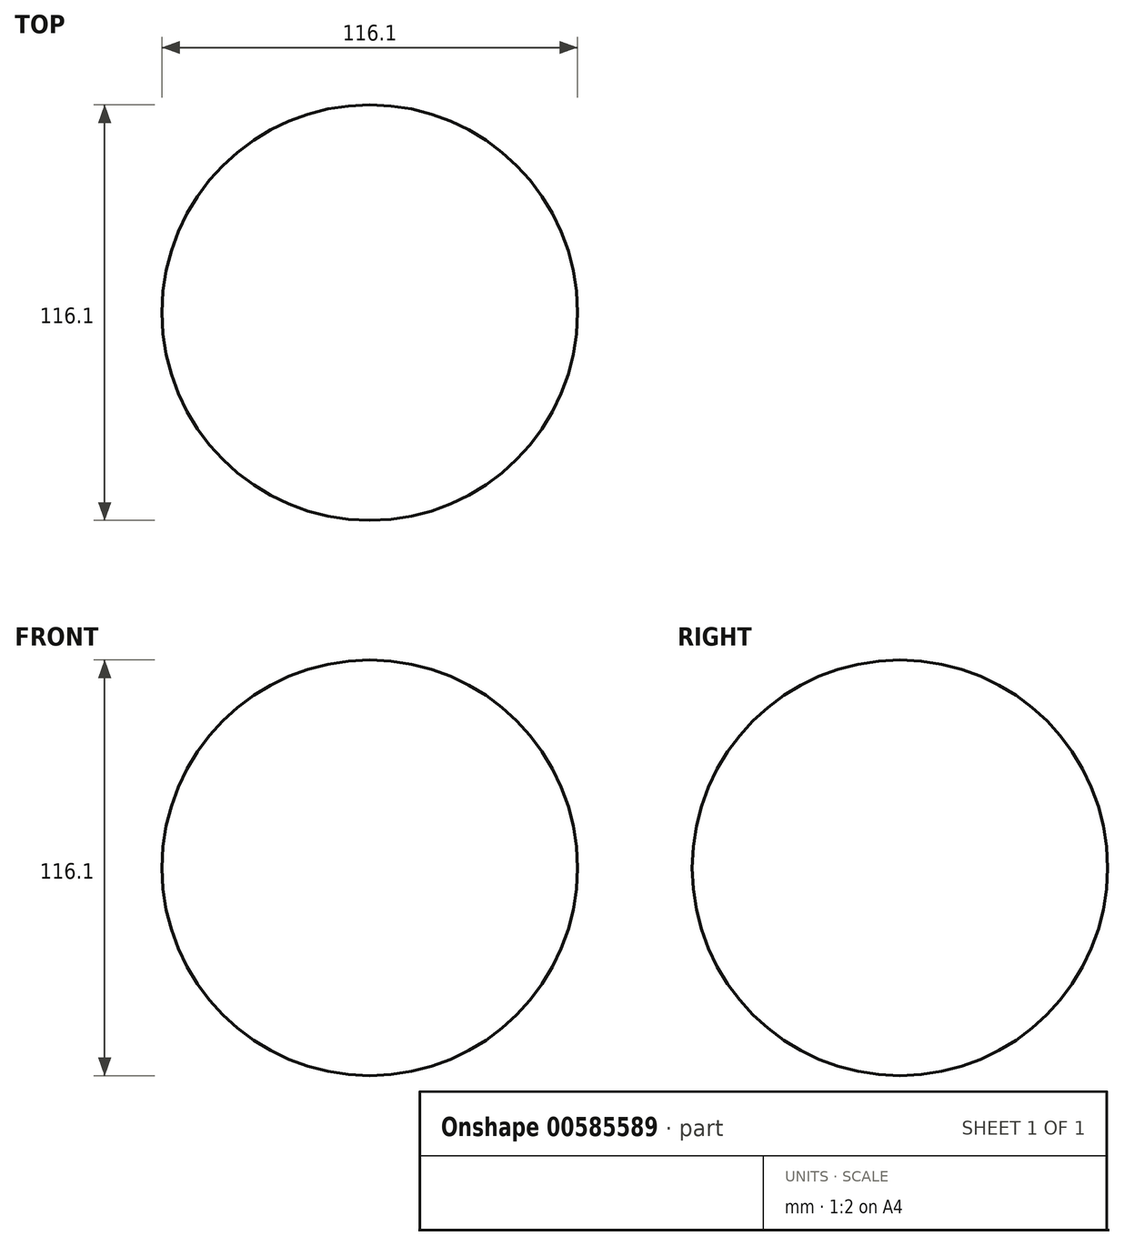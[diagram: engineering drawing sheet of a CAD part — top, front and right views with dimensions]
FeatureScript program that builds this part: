
annotation { "Feature Type Name" : "Feature", "Feature Type Description" : "" }
export const myFeature = defineFeature(function(context is Context, id is Id, definition is map)
    precondition{}
    {
        {
            var Q0;
            Q0=qCreatedBy(makeId("Front.planeOp"),FACE);
            var sketch = newSketch(context, id + "F0", { "sketchPlane" : qUnion([Q0])});
            skArc(sketch, "E0", {"start": v(-58.05, 0) * mm, "mid": v(0, 58.05) * mm, "end": v(58.05, 0) * mm});
            skSolve(sketch);
        }
        {
            var Q0;
            Q0=qCreatedBy(makeId("Front.planeOp"),FACE);
            var sketch = newSketch(context, id + "F1", { "sketchPlane" : qUnion([Q0])});
            skLineSegment(sketch, "E1", {"start": v(-74, 0) * mm, "end": v(69.24, 0) * mm});
            skSolve(sketch);
        }
        {
            var Q0;
            Q0=sQuery(id+"F0.wireOp",EDGE,"E0");
            var Q1;
            Q1=sQuery(id+"F1.wireOp",EDGE,"E1");
            revolve(context, id + "F2", {"bodyType" : ToolBodyType.SURFACE, "surfaceEntities" : qUnion([Q0]), "axis" : qUnion([Q1]), "revolveType" : RevolveType.FULL});
        }
    });
